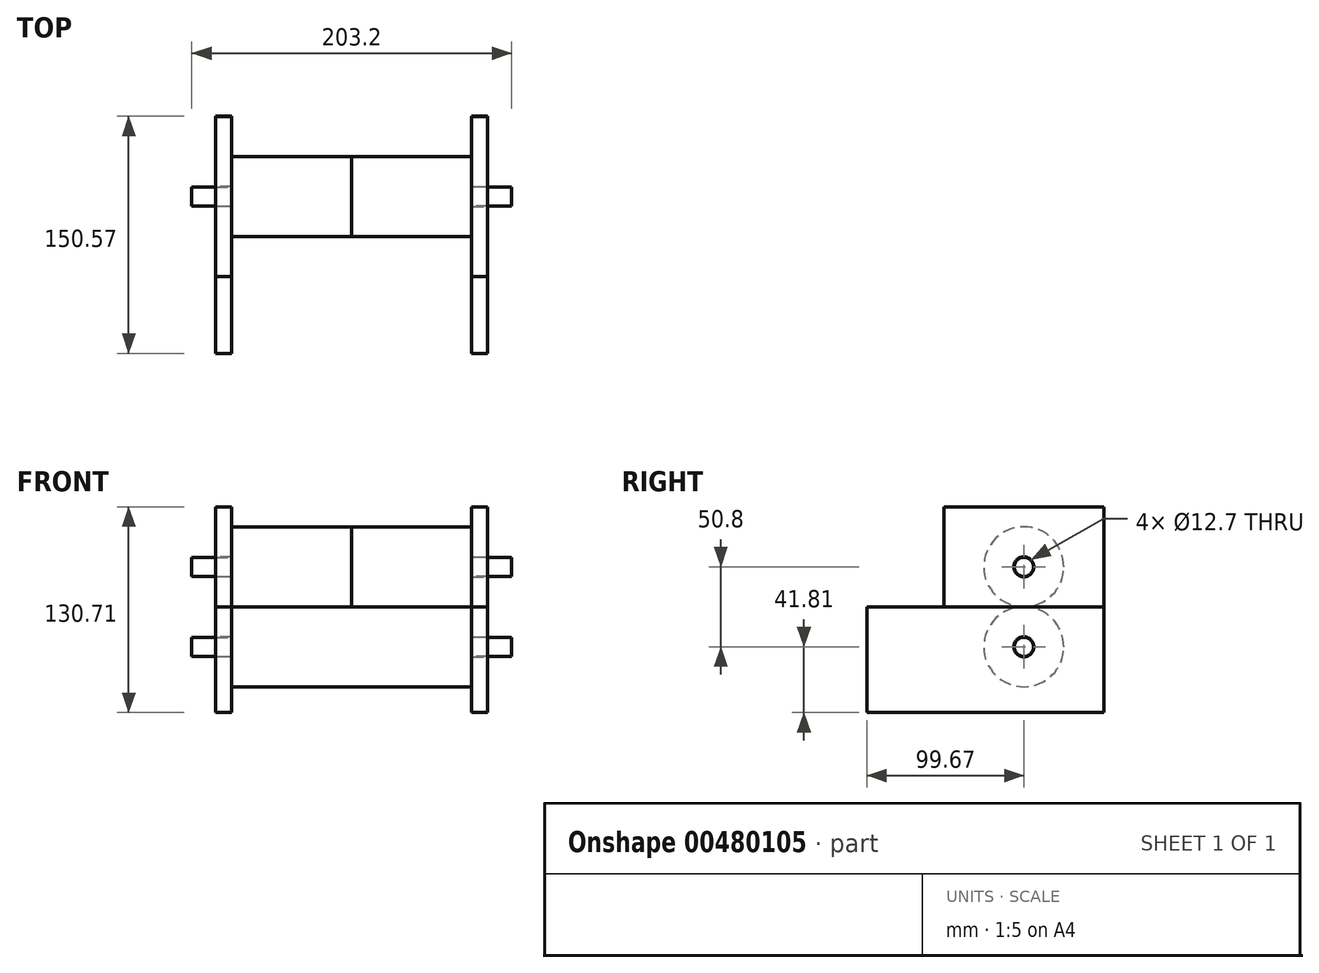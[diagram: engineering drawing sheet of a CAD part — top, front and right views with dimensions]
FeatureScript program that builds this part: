
annotation { "Feature Type Name" : "Feature", "Feature Type Description" : "" }
export const myFeature = defineFeature(function(context is Context, id is Id, definition is map)
    precondition{}
    {
        {
            var Q0;
            Q0=qCreatedBy(makeId("Right.planeOp"),FACE);
            var sketch = newSketch(context, id + "F0", { "sketchPlane" : qUnion([Q0])});
            skCircle(sketch, "E0", {"center": v(0, 25.4) * mm, "radius": 25.4 * mm});
            skCircle(sketch, "E1", {"center": v(0, -25.4) * mm, "radius": 25.4 * mm});
            skSolve(sketch);
        }
        {
            var Q0;
            Q0=makeQuery(id+"F0.imprint","IMPRINT",FACE,{"disambiguationData":[TD([[makeQuery(id+"F0.imprint","IMPRINT",EDGE,{"derivedFrom":sQuery(id+"F0.wireOp",EDGE,"E0")}),1.0]])]});
            var Q1;
            Q1=makeQuery(id+"F0.imprint","IMPRINT",FACE,{"disambiguationData":[TD([[makeQuery(id+"F0.imprint","IMPRINT",EDGE,{"derivedFrom":sQuery(id+"F0.wireOp",EDGE,"E1")}),1.0]])]});
            extrude(context, id + "F1", {"entities" : qUnion([Q0, Q1]), "depth" : 76.2 * mm});
        }
        {
            var Q0;
            Q0=makeQuery(id+"F1.opExtrude","CAP_FACE",FACE,{"disambiguationData":[OSD([sQuery(id+"F0.wireOp",EDGE,"E0")])],"isStart":false});
            cPlane(context, id + "F2", {"entities" : qUnion([Q0]), "cplaneType" : CPlaneType.OFFSET, "offset" : 0 * mm, "width" : 152.4 * mm, "height" : 152.4 * mm});
        }
        {
            var Q0;
            Q0=qCreatedBy(id+"F2.planeOp",FACE);
            var sketch = newSketch(context, id + "F3", { "sketchPlane" : qUnion([Q0])});
            skLineSegment(sketch, "E2.bottom", {"start": v(-50.8, 0) * mm, "end": v(50.8, 0) * mm});
            skLineSegment(sketch, "E2.top", {"start": v(-50.8, 63.5) * mm, "end": v(50.8, 63.5) * mm});
            skLineSegment(sketch, "E2.left", {"start": v(-50.8, 0) * mm, "end": v(-50.8, 63.5) * mm});
            skLineSegment(sketch, "E2.right", {"start": v(50.8, 0) * mm, "end": v(50.8, 63.5) * mm});
            skSolve(sketch);
        }
        {
            var Q0;
            Q0=makeQuery(id+"F3.imprint","IMPRINT",FACE,{"disambiguationData":[TD([[makeQuery(id+"F3.imprint","IMPRINT",EDGE,{"derivedFrom":sQuery(id+"F3.wireOp",EDGE,"E2.bottom")}),1.0]])]});
            extrude(context, id + "F4", {"entities" : qUnion([Q0]), "depth" : 10.16 * mm});
        }
        {
            var Q0;
            Q0=makeQuery(id+"F1.opExtrude","CAP_FACE",FACE,{"disambiguationData":[OSD([sQuery(id+"F0.wireOp",EDGE,"E1")])],"isStart":false});
            cPlane(context, id + "F5", {"entities" : qUnion([Q0]), "cplaneType" : CPlaneType.OFFSET, "offset" : 0 * mm, "width" : 152.4 * mm, "height" : 152.4 * mm});
        }
        {
            var Q0;
            Q0=qCreatedBy(id+"F5.planeOp",FACE);
            var sketch = newSketch(context, id + "F6", { "sketchPlane" : qUnion([Q0])});
            skLineSegment(sketch, "E3.bottom", {"start": v(50.9, 0) * mm, "end": v(-99.67, 0) * mm});
            skLineSegment(sketch, "E3.top", {"start": v(50.9, -67.2) * mm, "end": v(-99.67, -67.2) * mm});
            skLineSegment(sketch, "E3.left", {"start": v(50.9, 0) * mm, "end": v(50.9, -67.2) * mm});
            skLineSegment(sketch, "E3.right", {"start": v(-99.67, 0) * mm, "end": v(-99.67, -67.2) * mm});
            skSolve(sketch);
        }
        {
            var Q0;
            Q0=makeQuery(id+"F6.imprint","IMPRINT",FACE,{"disambiguationData":[TD([[makeQuery(id+"F6.imprint","IMPRINT",EDGE,{"derivedFrom":sQuery(id+"F6.wireOp",EDGE,"E3.bottom")}),1.0]])]});
            extrude(context, id + "F7", {"entities" : qUnion([Q0]), "depth" : 10.16 * mm});
        }
        {
            var Q0;
            Q0=makeQuery(id+"F1.opExtrude","SWEPT_BODY",BODY,{"disambiguationData":[OSD([sQuery(id+"F0.wireOp",EDGE,"E0")])]});
            var Q1;
            Q1=makeQuery(id+"F4.opExtrude","SWEPT_BODY",BODY,{"disambiguationData":[OSD([sQuery(id+"F3.wireOp",EDGE,"E2.bottom"),sQuery(id+"F3.wireOp",EDGE,"E2.top"),sQuery(id+"F3.wireOp",EDGE,"E2.left"),sQuery(id+"F3.wireOp",EDGE,"E2.right")])]});
            var Q2;
            Q2=makeQuery(id+"F7.opExtrude","SWEPT_BODY",BODY,{"disambiguationData":[OSD([sQuery(id+"F6.wireOp",EDGE,"E3.bottom"),sQuery(id+"F6.wireOp",EDGE,"E3.top"),sQuery(id+"F6.wireOp",EDGE,"E3.left"),sQuery(id+"F6.wireOp",EDGE,"E3.right")])]});
            var Q3;
            Q3=makeQuery(id+"F1.opExtrude","SWEPT_BODY",BODY,{"disambiguationData":[OSD([sQuery(id+"F0.wireOp",EDGE,"E1")])]});
            var Q4;
            Q4=qCreatedBy(makeId("Right.planeOp"),FACE);
            mirror(context, id + "F8", {"entities" : qUnion([Q0, Q1, Q2, Q3]), "mirrorPlane" : qUnion([Q4])});
        }
        {
            var Q0;
            Q0=makeQuery(id+"F8.opPattern","COPY",BODY,{"derivedFrom":makeQuery(id+"F1.opExtrude","SWEPT_BODY",BODY,{"disambiguationData":[OSD([sQuery(id+"F0.wireOp",EDGE,"E1")])]}),"instanceName":"1"});
            var Q1;
            Q1=makeQuery(id+"F1.opExtrude","SWEPT_BODY",BODY,{"disambiguationData":[OSD([sQuery(id+"F0.wireOp",EDGE,"E1")])]});
            booleanBodies(context, id + "F9", {"operationType" : BooleanOperationType.UNION, "tools" : qUnion([Q0, Q1])});
        }
        {
            var Q0;
            Q0=makeQuery(id+"F4.opExtrude","CAP_FACE",FACE,{"disambiguationData":[OSD([sQuery(id+"F3.wireOp",EDGE,"E2.bottom"),sQuery(id+"F3.wireOp",EDGE,"E2.top"),sQuery(id+"F3.wireOp",EDGE,"E2.left"),sQuery(id+"F3.wireOp",EDGE,"E2.right")])],"isStart":false});
            var sketch = newSketch(context, id + "F10", { "sketchPlane" : qUnion([Q0])});
            skSolve(sketch);
        }
        {
            var Q0;
            Q0=makeQuery(id+"F10.imprint","IMPRINT",FACE,{"disambiguationData":[TD([[makeQuery(id+"F10.imprint","IMPRINT",EDGE,{"derivedFrom":makeQuery(id+"F4.opExtrude","CAP_EDGE",EDGE,{"disambiguationData":[OSD([sQuery(id+"F3.wireOp",EDGE,"E2.bottom")])],"isStart":false})}),1.0]])]});
            var sketch = newSketch(context, id + "F11", { "sketchPlane" : qUnion([Q0])});
            skCircle(sketch, "E4.0", {"center": v(0, 25.4) * mm, "radius": 25.4 * mm, "construction": true});
            skCircle(sketch, "E5", {"center": v(0, 25.4) * mm, "radius": 6.35 * mm});
            skSolve(sketch);
        }
        {
            var Q0;
            Q0=makeQuery(id+"F11.imprint","IMPRINT",FACE,{"disambiguationData":[TD([[makeQuery(id+"F11.imprint","IMPRINT",EDGE,{"derivedFrom":sQuery(id+"F11.wireOp",EDGE,"E5")}),1.0]])]});
            var Q1;
            Q1=makeQuery(id+"F4.opExtrude","CAP_FACE",FACE,{"disambiguationData":[OSD([sQuery(id+"F3.wireOp",EDGE,"E2.bottom"),sQuery(id+"F3.wireOp",EDGE,"E2.top"),sQuery(id+"F3.wireOp",EDGE,"E2.left"),sQuery(id+"F3.wireOp",EDGE,"E2.right")])],"isStart":true});
            extrude(context, id + "F12", {"entities" : qUnion([Q0]), "operationType" : NewBodyOperationType.REMOVE, "endBound" : BoundingType.UP_TO_SURFACE, "oppositeDirection" : true, "endBoundEntityFace" : qUnion([Q1]), "depth" : 25.4 * mm});
        }
        {
            var Q0;
            Q0=makeQuery(id+"F8.opPattern","COPY",FACE,{"derivedFrom":makeQuery(id+"F4.opExtrude","CAP_FACE",FACE,{"disambiguationData":[OSD([sQuery(id+"F3.wireOp",EDGE,"E2.bottom"),sQuery(id+"F3.wireOp",EDGE,"E2.top"),sQuery(id+"F3.wireOp",EDGE,"E2.left"),sQuery(id+"F3.wireOp",EDGE,"E2.right")])],"isStart":false}),"instanceName":"1"});
            cPlane(context, id + "F13", {"entities" : qUnion([Q0]), "cplaneType" : CPlaneType.OFFSET, "offset" : 0 * mm, "width" : 152.4 * mm, "height" : 152.4 * mm});
        }
        {
            var Q0;
            Q0=qCreatedBy(id+"F13.planeOp",FACE);
            var sketch = newSketch(context, id + "F14", { "sketchPlane" : qUnion([Q0])});
            skCircle(sketch, "E6", {"center": v(0, 25.4) * mm, "radius": 6.35 * mm});
            skSolve(sketch);
        }
        {
            var Q0;
            Q0=makeQuery(id+"F14.imprint","IMPRINT",FACE,{"disambiguationData":[TD([[makeQuery(id+"F14.imprint","IMPRINT",EDGE,{"derivedFrom":sQuery(id+"F14.wireOp",EDGE,"E6")}),1.0]])]});
            extrude(context, id + "F15", {"entities" : qUnion([Q0]), "operationType" : NewBodyOperationType.REMOVE, "endBound" : BoundingType.UP_TO_NEXT, "oppositeDirection" : true, "depth" : 25.4 * mm, "offsetDistance" : 25.4 * mm});
        }
        {
            var Q0;
            Q0=qCreatedBy(id+"F13.planeOp",FACE);
            var sketch = newSketch(context, id + "F16", { "sketchPlane" : qUnion([Q0])});
            skCircle(sketch, "E7", {"center": v(0, -25.4) * mm, "radius": 6.35 * mm});
            skSolve(sketch);
        }
        {
            var Q0;
            Q0=makeQuery(id+"F16.imprint","IMPRINT",FACE,{"disambiguationData":[TD([[makeQuery(id+"F16.imprint","IMPRINT",EDGE,{"derivedFrom":sQuery(id+"F16.wireOp",EDGE,"E7")}),1.0]])]});
            extrude(context, id + "F17", {"entities" : qUnion([Q0]), "operationType" : NewBodyOperationType.REMOVE, "endBound" : BoundingType.UP_TO_NEXT, "oppositeDirection" : true, "depth" : 25.4 * mm, "offsetDistance" : 25.4 * mm});
        }
        {
            var Q0;
            Q0=makeQuery(id+"F7.opExtrude","CAP_FACE",FACE,{"disambiguationData":[OSD([sQuery(id+"F6.wireOp",EDGE,"E3.bottom"),sQuery(id+"F6.wireOp",EDGE,"E3.top"),sQuery(id+"F6.wireOp",EDGE,"E3.left"),sQuery(id+"F6.wireOp",EDGE,"E3.right")])],"isStart":false});
            cPlane(context, id + "F18", {"entities" : qUnion([Q0]), "cplaneType" : CPlaneType.OFFSET, "offset" : 0 * mm, "width" : 152.4 * mm, "height" : 152.4 * mm});
        }
        {
            var Q0;
            Q0=qCreatedBy(id+"F18.planeOp",FACE);
            var sketch = newSketch(context, id + "F19", { "sketchPlane" : qUnion([Q0])});
            skCircle(sketch, "E8", {"center": v(0, -25.4) * mm, "radius": 6.35 * mm});
            skSolve(sketch);
        }
        {
            var Q0;
            Q0=makeQuery(id+"F19.imprint","IMPRINT",FACE,{"disambiguationData":[TD([[makeQuery(id+"F19.imprint","IMPRINT",EDGE,{"derivedFrom":sQuery(id+"F19.wireOp",EDGE,"E8")}),1.0]])]});
            extrude(context, id + "F20", {"entities" : qUnion([Q0]), "operationType" : NewBodyOperationType.REMOVE, "endBound" : BoundingType.UP_TO_NEXT, "oppositeDirection" : true, "depth" : 25.4 * mm, "offsetDistance" : 25.4 * mm});
        }
        {
            var Q0;
            Q0=qCreatedBy(id+"F2.planeOp",FACE);
            var sketch = newSketch(context, id + "F21", { "sketchPlane" : qUnion([Q0])});
            skCircle(sketch, "E9", {"center": v(0, 25.4) * mm, "radius": 6.1 * mm});
            skSolve(sketch);
        }
        {
            var Q0;
            Q0 = qSketchRegion(id + "F21", true);
            extrude(context, id + "F22", {"entities" : qUnion([Q0]), "operationType" : NewBodyOperationType.ADD, "depth" : 25.4 * mm, "offsetDistance" : 25.4 * mm});
        }
        {
            var Q0;
            Q0=qCreatedBy(id+"F5.planeOp",FACE);
            var sketch = newSketch(context, id + "F23", { "sketchPlane" : qUnion([Q0])});
            skCircle(sketch, "E10", {"center": v(0, -25.4) * mm, "radius": 6.1 * mm});
            skSolve(sketch);
        }
        {
            var Q0;
            Q0 = qSketchRegion(id + "F23", true);
            extrude(context, id + "F24", {"entities" : qUnion([Q0]), "operationType" : NewBodyOperationType.ADD, "depth" : 25.4 * mm, "offsetDistance" : 25.4 * mm});
        }
        {
            var Q0;
            Q0=makeQuery(id+"F8.opPattern","COPY",FACE,{"derivedFrom":makeQuery(id+"F7.opExtrude","CAP_FACE",FACE,{"disambiguationData":[OSD([sQuery(id+"F6.wireOp",EDGE,"E3.bottom"),sQuery(id+"F6.wireOp",EDGE,"E3.top"),sQuery(id+"F6.wireOp",EDGE,"E3.left"),sQuery(id+"F6.wireOp",EDGE,"E3.right")])],"isStart":true}),"instanceName":"1"});
            cPlane(context, id + "F25", {"entities" : qUnion([Q0]), "cplaneType" : CPlaneType.OFFSET, "offset" : 0 * mm, "width" : 152.4 * mm, "height" : 152.4 * mm});
        }
        {
            var Q0;
            Q0=qCreatedBy(id+"F25.planeOp",FACE);
            var sketch = newSketch(context, id + "F26", { "sketchPlane" : qUnion([Q0])});
            skCircle(sketch, "E11", {"center": v(0, -25.4) * mm, "radius": 6.1 * mm});
            skSolve(sketch);
        }
        {
            var Q0;
            Q0 = qSketchRegion(id + "F26", true);
            extrude(context, id + "F27", {"entities" : qUnion([Q0]), "operationType" : NewBodyOperationType.ADD, "oppositeDirection" : true, "depth" : 25.4 * mm, "offsetDistance" : 25.4 * mm});
        }
        {
            var Q0;
            Q0=makeQuery(id+"F8.opPattern","COPY",FACE,{"derivedFrom":makeQuery(id+"F4.opExtrude","CAP_FACE",FACE,{"disambiguationData":[OSD([sQuery(id+"F3.wireOp",EDGE,"E2.bottom"),sQuery(id+"F3.wireOp",EDGE,"E2.top"),sQuery(id+"F3.wireOp",EDGE,"E2.left"),sQuery(id+"F3.wireOp",EDGE,"E2.right")])],"isStart":true}),"instanceName":"1"});
            cPlane(context, id + "F28", {"entities" : qUnion([Q0]), "cplaneType" : CPlaneType.OFFSET, "offset" : 0 * mm, "width" : 152.4 * mm, "height" : 152.4 * mm});
        }
        {
            var Q0;
            Q0=qCreatedBy(id+"F28.planeOp",FACE);
            var sketch = newSketch(context, id + "F29", { "sketchPlane" : qUnion([Q0])});
            skCircle(sketch, "E12", {"center": v(0, 25.4) * mm, "radius": 6.1 * mm});
            skSolve(sketch);
        }
        {
            var Q0;
            Q0 = qSketchRegion(id + "F29", true);
            extrude(context, id + "F30", {"entities" : qUnion([Q0]), "operationType" : NewBodyOperationType.ADD, "oppositeDirection" : true, "depth" : 25.4 * mm, "offsetDistance" : 25.4 * mm});
        }
    });
